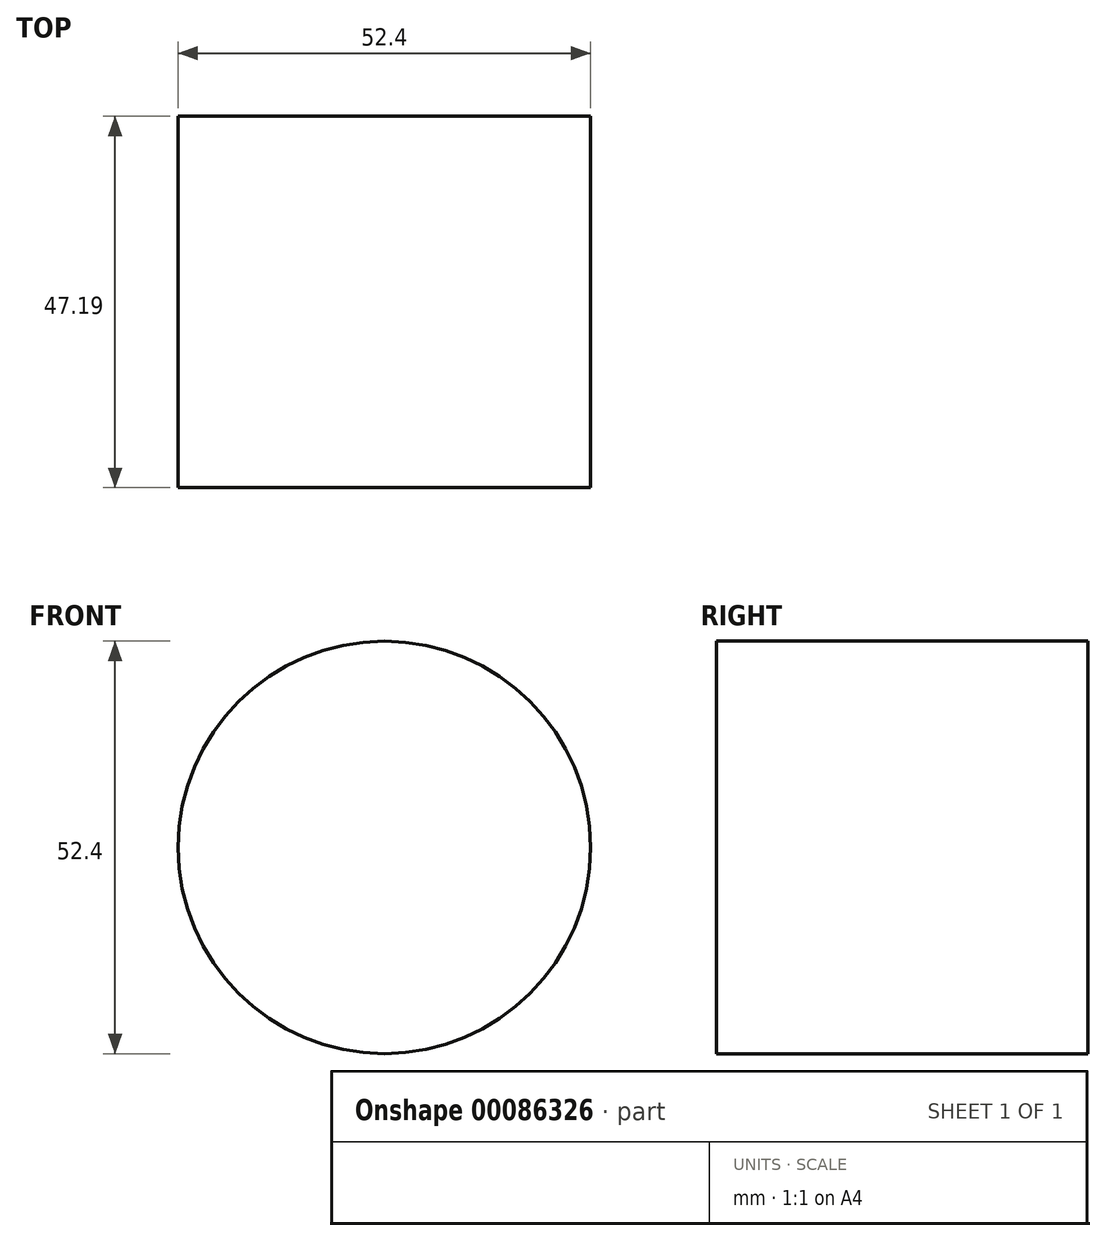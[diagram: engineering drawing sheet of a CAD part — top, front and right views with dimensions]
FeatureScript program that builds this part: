
annotation { "Feature Type Name" : "Feature", "Feature Type Description" : "" }
export const myFeature = defineFeature(function(context is Context, id is Id, definition is map)
    precondition{}
    {
        {
            var Q0;
            Q0=qCreatedBy(makeId("Front.planeOp"),FACE);
            var sketch = newSketch(context, id + "F0", { "sketchPlane" : qUnion([Q0])});
            skCircle(sketch, "E0", {"center": v(0, 0) * mm, "radius": 26.2 * mm});
            skSolve(sketch);
        }
        {
            var Q0;
            Q0=makeQuery(id+"F0.imprint","IMPRINT",FACE,{"disambiguationData":[TD([[makeQuery(id+"F0.imprint","IMPRINT",EDGE,{"derivedFrom":sQuery(id+"F0.wireOp",EDGE,"E0")}),1.0]])]});
            extrude(context, id + "F1", {"entities" : qUnion([Q0]), "depth" : 47.2 * mm});
        }
    });
